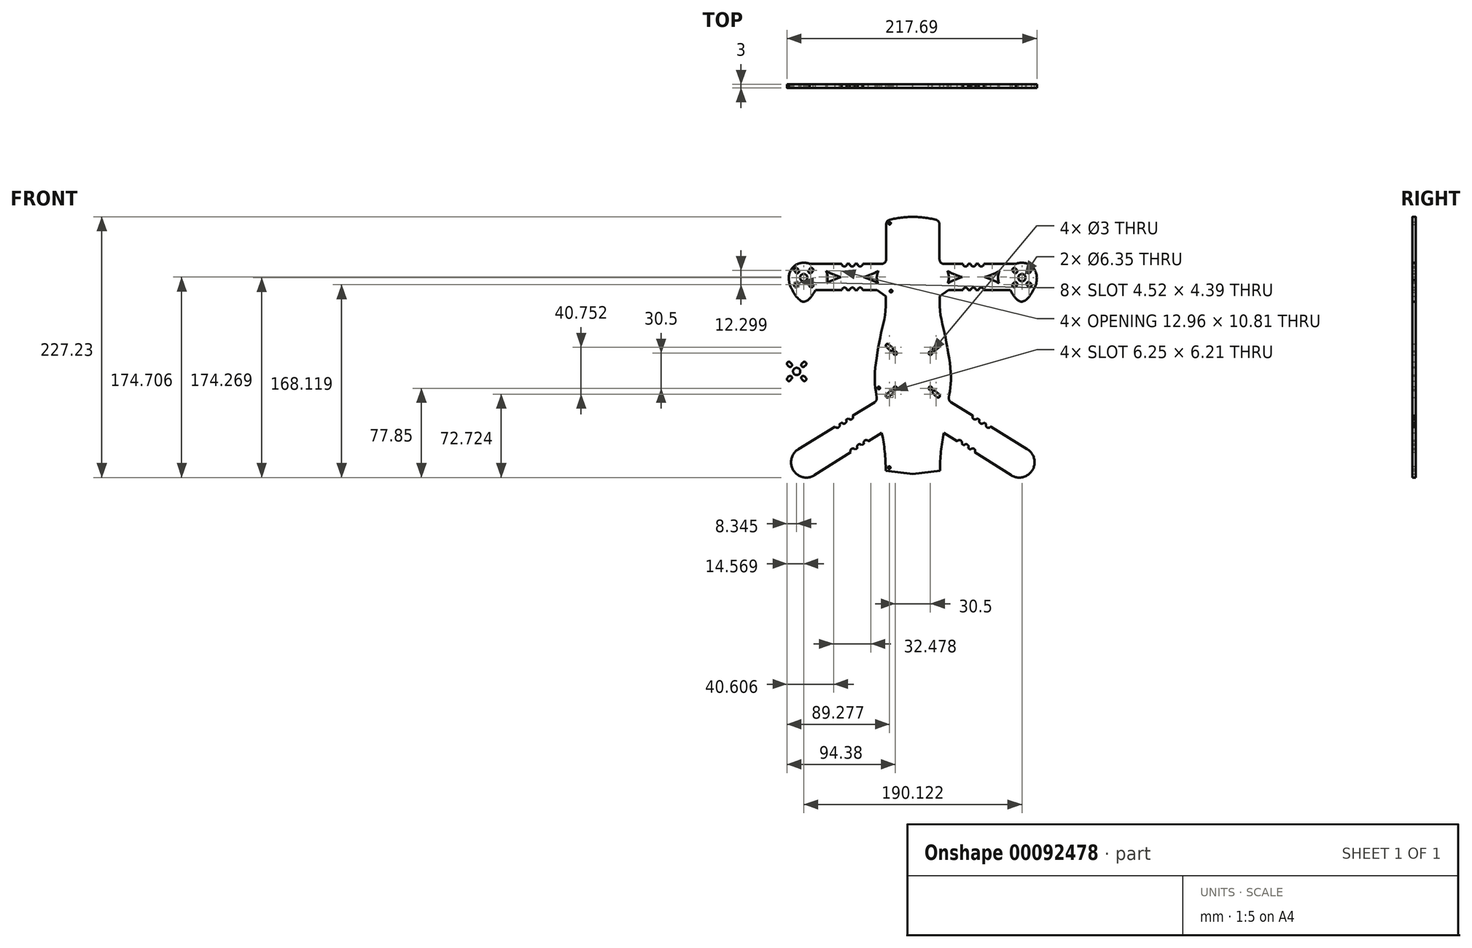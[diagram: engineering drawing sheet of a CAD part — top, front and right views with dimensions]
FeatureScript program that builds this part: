
annotation { "Feature Type Name" : "Feature", "Feature Type Description" : "" }
export const myFeature = defineFeature(function(context is Context, id is Id, definition is map)
    precondition{}
    {
        {
            var Q0;
            Q0=qCreatedBy(makeId("Front.planeOp"),FACE);
            var sketch = newSketch(context, id + "F0", { "sketchPlane" : qUnion([Q0])});
            skArc(sketch, "E0", {"start": v(-89.84, 93.07) * mm, "mid": v(-102.97, 91.49) * mm, "end": v(-107.91, 79.22) * mm});
            skLineSegment(sketch, "E1", {"start": v(-89.84, 93.07) * mm, "end": v(-68.74, 93.07) * mm});
            skLineSegment(sketch, "E2", {"start": v(-84.98, 70.21) * mm, "end": v(-68.66, 70.21) * mm});
            skCircle(sketch, "E3", {"center": v(-95.06, 81.17) * mm, "radius": 63.5 * mm, "construction": true});
            skCircle(sketch, "E4", {"center": v(-92.79, -79.8) * mm, "radius": 63.5 * mm, "construction": true});
            skLineSegment(sketch, "E5.trimOffspring", {"start": v(-27, 67.39) * mm, "end": v(-27, 67.4) * mm});
            skArc(sketch, "E6", {"start": v(0, 134.13) * mm, "mid": v(-10.16, 133.5) * mm, "end": v(-20.15, 131.58) * mm});
            skLineSegment(sketch, "E7", {"start": v(-104.2, 69.27) * mm, "end": v(-104.2, 69.27) * mm});
            skFitSpline(sketch, "E8.trimOffspring", {"points": [v(-82.06, 81.17) * mm, v(-83.74, 72.94) * mm, v(-95.05, 60.22) * mm, v(-105.53, 73.45) * mm, v(-110.06, 81.17) * mm], "startDerivative": vector(-2.07, -33.38) * mm, "endDerivative": vector(-8.03, 30.88) * mm});
            skFitSpline(sketch, "E9.MirrorCS", {"points": [v(-107.91, 79.22) * mm, v(-106.3, 72.94) * mm, v(-95.05, 60.22) * mm, v(-84.6, 73.45) * mm, v(-82.06, 81.17) * mm], "startDerivative": vector(2.07, -33.38) * mm, "endDerivative": vector(8.03, 30.88) * mm});
            skLineSegment(sketch, "E10.trimOffspring", {"start": v(-95.06, 68.17) * mm, "end": v(-95.06, 68.16) * mm});
            skLineSegment(sketch, "E11.trimOffspring", {"start": v(-102.98, 70.86) * mm, "end": v(-102.98, 70.86) * mm});
            skFitSpline(sketch, "E12.trimOffspring", {"points": [v(-82.07, 81.2) * mm, v(-83.75, 72.93) * mm, v(-95.05, 60.22) * mm, v(-105.53, 73.45) * mm, v(-108.06, 81.16) * mm], "startDerivative": vector(-2.07, -33.38) * mm, "endDerivative": vector(-8.03, 30.88) * mm});
            skPoint(sketch, "E13.visualSharp", {"position": v(-27.02, 93.07) * mm});
            skArc(sketch, "E13.filletArc", {"start": v(-27.02, 96.91) * mm, "mid": v(-27.02, 97) * mm, "end": v(-27.02, 97.07) * mm});
            skLineSegment(sketch, "E14.MirrorCS", {"start": v(27.02, 126.57) * mm, "end": v(27.02, 126.57) * mm});
            skLineSegment(sketch, "E15.MirrorCS", {"start": v(25.72, 29.34) * mm, "end": v(25.72, 29.34) * mm});
            skCircle(sketch, "E16.MirrorC", {"center": v(92.79, -79.8) * mm, "radius": 63.5 * mm, "construction": true});
            skLineSegment(sketch, "E17.MirrorCS", {"start": v(33.17, -57.94) * mm, "end": v(30.27, -56.1) * mm});
            skArc(sketch, "E18.MirrorCS", {"start": v(99.78, -68.48) * mm, "mid": v(104.07, -86.84) * mm, "end": v(85.7, -91.05) * mm});
            skCircle(sketch, "E19.MirrorC", {"center": v(95.06, 81.17) * mm, "radius": 63.5 * mm, "construction": true});
            skPoint(sketch, "E20.end.orphan", {"position": v(0, 134.13) * mm});
            skArc(sketch, "E21", {"start": v(-55, 93.07) * mm, "mid": v(-52.79, 90.85) * mm, "end": v(-50.56, 93.07) * mm});
            skArc(sketch, "E22", {"start": v(-61.87, 93.07) * mm, "mid": v(-59.65, 90.85) * mm, "end": v(-57.43, 93.07) * mm});
            skPoint(sketch, "E23.center.orphan", {"position": v(-59.65, 92.47) * mm});
            skLineSegment(sketch, "E24.trimOffspring", {"start": v(-64.3, 93.07) * mm, "end": v(-61.87, 93.07) * mm});
            skLineSegment(sketch, "E25.trimOffspring", {"start": v(-57.43, 93.07) * mm, "end": v(-55, 93.07) * mm});
            skCircle(sketch, "E26", {"center": v(-37.46, 81.64) * mm, "radius": 13.12 * mm, "construction": true});
            skPoint(sketch, "E26.second.point", {"position": v(-31.02, 70.21) * mm});
            skPoint(sketch, "E26.third.point", {"position": v(-50.56, 82.35) * mm});
            skArc(sketch, "E27.MirrorCS", {"start": v(-61.79, 70.21) * mm, "mid": v(-59.56, 72.44) * mm, "end": v(-57.34, 70.21) * mm});
            skArc(sketch, "E28.MirrorCS", {"start": v(-54.92, 70.21) * mm, "mid": v(-52.7, 72.44) * mm, "end": v(-50.48, 70.21) * mm});
            skLineSegment(sketch, "E29.trimOffspring", {"start": v(-64.2, 70.21) * mm, "end": v(-61.79, 70.21) * mm});
            skLineSegment(sketch, "E30.trimOffspring", {"start": v(-57.34, 70.21) * mm, "end": v(-54.92, 70.21) * mm});
            skLineSegment(sketch, "E31.trimOffspring", {"start": v(-50.48, 70.21) * mm, "end": v(-48.14, 70.21) * mm});
            skLineSegment(sketch, "E32.MirrorCS", {"start": v(-99.78, -68.48) * mm, "end": v(-73.61, -52.32) * mm});
            skLineSegment(sketch, "E33.MirrorCS", {"start": v(-85.7, -91.05) * mm, "end": v(-59.85, -74.76) * mm});
            skArc(sketch, "E34.MirrorCS", {"start": v(-99.78, -68.48) * mm, "mid": v(-104.07, -86.84) * mm, "end": v(-85.7, -91.05) * mm});
            skArc(sketch, "E35", {"start": v(-67.78, -48.72) * mm, "mid": v(-64.72, -49.44) * mm, "end": v(-64, -46.38) * mm});
            skArc(sketch, "E36", {"start": v(-61.94, -45.11) * mm, "mid": v(-58.88, -45.83) * mm, "end": v(-58.15, -42.77) * mm});
            skLineSegment(sketch, "E37.trimOffspring", {"start": v(-64, -46.38) * mm, "end": v(-61.94, -45.11) * mm});
            skLineSegment(sketch, "E38.trimOffspring", {"start": v(-69.83, -49.98) * mm, "end": v(-67.78, -48.72) * mm});
            skLineSegment(sketch, "E39.trimOffspring", {"start": v(-58.15, -42.77) * mm, "end": v(-56.1, -41.5) * mm});
            skArc(sketch, "E40.MirrorCS", {"start": v(-54.05, -71.1) * mm, "mid": v(-53.34, -68.05) * mm, "end": v(-50.29, -68.73) * mm});
            skArc(sketch, "E41.MirrorCS", {"start": v(-48.24, -67.44) * mm, "mid": v(-47.54, -64.4) * mm, "end": v(-44.48, -65.07) * mm});
            skLineSegment(sketch, "E42.trimOffspring", {"start": v(-56.09, -72.39) * mm, "end": v(-54.05, -71.1) * mm});
            skLineSegment(sketch, "E43.trimOffspring", {"start": v(-50.29, -68.73) * mm, "end": v(-48.24, -67.44) * mm});
            skLineSegment(sketch, "E44.trimOffspring", {"start": v(-44.48, -65.07) * mm, "end": v(-42.46, -63.8) * mm});
            skArc(sketch, "E45.MirrorCS", {"start": v(61.94, -45.11) * mm, "mid": v(58.88, -45.83) * mm, "end": v(58.15, -42.77) * mm});
            skLineSegment(sketch, "E46.MirrorCS", {"start": v(64, -46.38) * mm, "end": v(61.94, -45.11) * mm});
            skArc(sketch, "E47.MirrorCS", {"start": v(67.78, -48.72) * mm, "mid": v(64.72, -49.44) * mm, "end": v(64, -46.38) * mm});
            skLineSegment(sketch, "E48.MirrorCS", {"start": v(69.83, -49.98) * mm, "end": v(67.78, -48.72) * mm});
            skLineSegment(sketch, "E49.MirrorCS", {"start": v(99.78, -68.48) * mm, "end": v(73.61, -52.32) * mm});
            skLineSegment(sketch, "E50.MirrorCS", {"start": v(44.48, -65.07) * mm, "end": v(42.46, -63.8) * mm});
            skArc(sketch, "E51.MirrorCS", {"start": v(48.24, -67.44) * mm, "mid": v(47.54, -64.4) * mm, "end": v(44.48, -65.07) * mm});
            skLineSegment(sketch, "E52.MirrorCS", {"start": v(50.29, -68.73) * mm, "end": v(48.24, -67.44) * mm});
            skArc(sketch, "E53.MirrorCS", {"start": v(54.05, -71.1) * mm, "mid": v(53.34, -68.05) * mm, "end": v(50.29, -68.73) * mm});
            skLineSegment(sketch, "E54.MirrorCS", {"start": v(56.09, -72.39) * mm, "end": v(54.05, -71.1) * mm});
            skLineSegment(sketch, "E55.MirrorCS", {"start": v(85.7, -91.05) * mm, "end": v(59.85, -74.76) * mm});
            skLineSegment(sketch, "E56.MirrorCS", {"start": v(-27.02, -119.64) * mm, "end": v(-26.92, -119.64) * mm});
            skLineSegment(sketch, "E57", {"start": v(0, -156.72) * mm, "end": v(0, 138.64) * mm, "construction": true});
            skLineSegment(sketch, "E58.MirrorCS", {"start": v(50.48, 70.21) * mm, "end": v(48.14, 70.21) * mm});
            skArc(sketch, "E59.MirrorCS", {"start": v(54.92, 70.21) * mm, "mid": v(52.7, 72.44) * mm, "end": v(50.48, 70.21) * mm});
            skLineSegment(sketch, "E60.MirrorCS", {"start": v(57.34, 70.21) * mm, "end": v(54.92, 70.21) * mm});
            skArc(sketch, "E61.MirrorCS", {"start": v(61.79, 70.21) * mm, "mid": v(59.56, 72.44) * mm, "end": v(57.34, 70.21) * mm});
            skLineSegment(sketch, "E62.MirrorCS", {"start": v(64.2, 70.21) * mm, "end": v(61.79, 70.21) * mm});
            skLineSegment(sketch, "E63.MirrorCS", {"start": v(84.98, 70.21) * mm, "end": v(68.66, 70.21) * mm});
            skFitSpline(sketch, "E64.MirrorCS", {"points": [v(82.07, 81.2) * mm, v(83.75, 72.93) * mm, v(95.05, 60.22) * mm, v(105.53, 73.45) * mm, v(108.06, 81.16) * mm], "startDerivative": vector(2.07, -33.38) * mm, "endDerivative": vector(8.03, 30.88) * mm});
            skFitSpline(sketch, "E65.MirrorCS", {"points": [v(107.91, 79.22) * mm, v(106.3, 72.94) * mm, v(95.05, 60.22) * mm, v(84.6, 73.45) * mm, v(82.06, 81.17) * mm], "startDerivative": vector(-2.07, -33.38) * mm, "endDerivative": vector(-8.03, 30.88) * mm});
            skArc(sketch, "E66.MirrorCS", {"start": v(89.84, 93.07) * mm, "mid": v(102.97, 91.49) * mm, "end": v(107.91, 79.22) * mm});
            skLineSegment(sketch, "E67.MirrorCS", {"start": v(89.84, 93.07) * mm, "end": v(68.74, 93.07) * mm});
            skLineSegment(sketch, "E68.MirrorCS", {"start": v(64.3, 93.07) * mm, "end": v(61.87, 93.07) * mm});
            skArc(sketch, "E69.MirrorCS", {"start": v(61.87, 93.07) * mm, "mid": v(59.65, 90.85) * mm, "end": v(57.43, 93.07) * mm});
            skLineSegment(sketch, "E70.MirrorCS", {"start": v(57.43, 93.07) * mm, "end": v(55, 93.07) * mm});
            skArc(sketch, "E71.MirrorCS", {"start": v(55, 93.07) * mm, "mid": v(52.79, 90.85) * mm, "end": v(50.56, 93.07) * mm});
            skLineSegment(sketch, "E72.MirrorCS", {"start": v(50.56, 93.07) * mm, "end": v(48.14, 93.07) * mm});
            skLineSegment(sketch, "E73", {"start": v(-27, 67.4) * mm, "end": v(-31.02, 70.21) * mm});
            skLineSegment(sketch, "E74.MirrorCS", {"start": v(27, 67.4) * mm, "end": v(31.02, 70.21) * mm});
            skLineSegment(sketch, "E75.trimOffspring", {"start": v(27, 70.21) * mm, "end": v(26.91, 70.21) * mm});
            skLineSegment(sketch, "E76.trimOffspring", {"start": v(27, 70.21) * mm, "end": v(27, 70.21) * mm});
            skLineSegment(sketch, "E77.bottom", {"start": v(-15.25, -15.25) * mm, "end": v(15.25, -15.25) * mm, "construction": true});
            skLineSegment(sketch, "E77.top", {"start": v(-15.25, 15.25) * mm, "end": v(15.25, 15.25) * mm, "construction": true});
            skLineSegment(sketch, "E77.left", {"start": v(-15.25, -15.25) * mm, "end": v(-15.25, 15.25) * mm, "construction": true});
            skLineSegment(sketch, "E77.right", {"start": v(15.25, -15.25) * mm, "end": v(15.25, 15.25) * mm, "construction": true});
            skPoint(sketch, "E77.middle", {"position": v(0, 0) * mm});
            skCircle(sketch, "E78", {"center": v(-15.25, 15.25) * mm, "radius": 1.5 * mm});
            skCircle(sketch, "E79", {"center": v(-15.25, -15.25) * mm, "radius": 1.5 * mm});
            skCircle(sketch, "E80", {"center": v(15.25, -15.25) * mm, "radius": 1.5 * mm});
            skCircle(sketch, "E81", {"center": v(15.25, 15.25) * mm, "radius": 1.5 * mm});
            skPoint(sketch, "E82.orphan", {"position": v(27, 67.4) * mm});
            skLineSegment(sketch, "E83", {"start": v(-33.17, -57.94) * mm, "end": v(-27, -54.05) * mm});
            skLineSegment(sketch, "E84", {"start": v(-39.84, -31.46) * mm, "end": v(-33.24, -27.38) * mm});
            skLineSegment(sketch, "E85", {"start": v(-27, 67.4) * mm, "end": v(-23.43, 64.9) * mm});
            skLineSegment(sketch, "E86", {"start": v(-31.02, 93.07) * mm, "end": v(-27.28, 93.07) * mm});
            skArc(sketch, "E87", {"start": v(-27, -120.02) * mm, "mid": v(-26.96, -119.83) * mm, "end": v(-26.92, -119.64) * mm});
            skFitSpline(sketch, "E88", {"points": [v(-30.93, -25.96) * mm, v(-31.88, -20.43) * mm, v(-32.97, -11.05) * mm, v(-32.97, 0) * mm, v(-30.51, 17.65) * mm, v(-27.02, 35.59) * mm, v(-24.06, 49.37) * mm, v(-23.43, 65.59) * mm], "startDerivative": vector(-9.96, 54.34) * mm, "endDerivative": vector(-0.3, 104.07) * mm});
            skLineSegment(sketch, "E89", {"start": v(-23.29, 97.04) * mm, "end": v(-23.14, 127.74) * mm});
            skPoint(sketch, "E89.startSnap0", {"position": v(-29, 68.8) * mm});
            skPoint(sketch, "E90.filletArc.center.orphan", {"position": v(-23.02, 126.6) * mm});
            skPoint(sketch, "E91.end.orphan", {"position": v(-27.02, 126.57) * mm});
            skPoint(sketch, "E92.newPointB", {"position": v(-23.43, 68.8) * mm});
            skArc(sketch, "E92.filletArc", {"start": v(-27.28, 93.07) * mm, "mid": v(-24.46, 94.23) * mm, "end": v(-23.29, 97.04) * mm});
            skArc(sketch, "E93.filletArc", {"start": v(-20.15, 131.58) * mm, "mid": v(-22.3, 130.17) * mm, "end": v(-23.14, 127.74) * mm});
            skPoint(sketch, "E94.0.internal.orphan", {"position": v(-26.91, 70.21) * mm});
            skPoint(sketch, "E94.7.internal.orphan", {"position": v(-32.97, -21.49) * mm});
            skPoint(sketch, "E94.8.internal.orphan", {"position": v(-26.91, -50.04) * mm});
            skPoint(sketch, "E95.startSnap0", {"position": v(-23.62, -87.03) * mm});
            skArc(sketch, "E96.trimOffspring", {"start": v(-23.62, -87.03) * mm, "mid": v(-24.47, -70.45) * mm, "end": v(-27, -54.05) * mm});
            skPoint(sketch, "E97.MirrorCS.end.orphan", {"position": v(0, -119.64) * mm});
            skPoint(sketch, "E98.orphan", {"position": v(27.02, 97.07) * mm});
            skPoint(sketch, "E99.MirrorCS.start.orphan", {"position": v(31.02, 93.07) * mm});
            skLineSegment(sketch, "E100.MirrorCS", {"start": v(39.84, -31.46) * mm, "end": v(33.24, -27.38) * mm});
            skArc(sketch, "E101.MirrorCS", {"start": v(23.62, -87.03) * mm, "mid": v(24.47, -70.45) * mm, "end": v(27, -54.05) * mm});
            skLineSegment(sketch, "E102.MirrorCS", {"start": v(33.17, -57.94) * mm, "end": v(27, -54.05) * mm});
            skFitSpline(sketch, "E103.MirrorCS", {"points": [v(30.93, -25.96) * mm, v(31.88, -20.43) * mm, v(32.97, -11.05) * mm, v(32.97, 0) * mm, v(30.51, 17.65) * mm, v(27.02, 35.59) * mm, v(24.06, 49.37) * mm, v(23.43, 65.59) * mm], "startDerivative": vector(9.96, 54.34) * mm, "endDerivative": vector(0.3, 104.07) * mm});
            skLineSegment(sketch, "E104.MirrorCS", {"start": v(27, 67.4) * mm, "end": v(23.43, 64.9) * mm});
            skArc(sketch, "E105.MirrorCS", {"start": v(27.28, 93.07) * mm, "mid": v(24.46, 94.23) * mm, "end": v(23.29, 97.04) * mm});
            skLineSegment(sketch, "E106.MirrorCS", {"start": v(23.29, 97.04) * mm, "end": v(23.14, 127.74) * mm});
            skArc(sketch, "E107.MirrorCS", {"start": v(0, 134.13) * mm, "mid": v(10.16, 133.5) * mm, "end": v(20.15, 131.58) * mm});
            skArc(sketch, "E108.MirrorCS", {"start": v(20.15, 131.58) * mm, "mid": v(22.3, 130.17) * mm, "end": v(23.14, 127.74) * mm});
            skLineSegment(sketch, "E109.MirrorCS", {"start": v(31.02, 93.07) * mm, "end": v(27.28, 93.07) * mm});
            skPoint(sketch, "E110.orphan", {"position": v(24.14, -87.03) * mm});
            skLineSegment(sketch, "E111", {"start": v(-23.62, -87.03) * mm, "end": v(0, -90.1) * mm});
            skLineSegment(sketch, "E112", {"start": v(0, -90.1) * mm, "end": v(23.62, -87.03) * mm});
            skArc(sketch, "E113.filletArc", {"start": v(-33.24, -27.38) * mm, "mid": v(-31.7, -25.63) * mm, "end": v(-31.4, -23.3) * mm});
            skArc(sketch, "E114.filletArc", {"start": v(31.4, -23.3) * mm, "mid": v(31.7, -25.63) * mm, "end": v(33.24, -27.38) * mm});
            skLineSegment(sketch, "E115.bottom", {"start": v(-101.78, 74.46) * mm, "end": v(-88.34, 74.46) * mm, "construction": true});
            skLineSegment(sketch, "E115.top", {"start": v(-101.78, 87.88) * mm, "end": v(-88.34, 87.88) * mm, "construction": true});
            skLineSegment(sketch, "E115.left", {"start": v(-101.78, 74.46) * mm, "end": v(-101.78, 87.88) * mm, "construction": true});
            skLineSegment(sketch, "E115.right", {"start": v(-88.34, 74.46) * mm, "end": v(-88.34, 87.88) * mm, "construction": true});
            skArc(sketch, "E116", {"start": v(-100.5, 89) * mm, "mid": v(-102.9, 89.16) * mm, "end": v(-103.06, 86.76) * mm});
            skArc(sketch, "E117", {"start": v(-89.61, 73.33) * mm, "mid": v(-87.21, 73.18) * mm, "end": v(-87.07, 75.58) * mm});
            skArc(sketch, "E118", {"start": v(-103.06, 75.58) * mm, "mid": v(-102.9, 73.18) * mm, "end": v(-100.5, 73.33) * mm});
            skCircle(sketch, "E119", {"center": v(-95.06, 81.17) * mm, "radius": 3.18 * mm});
            skArc(sketch, "E120", {"start": v(-102.06, 85.63) * mm, "mid": v(-99.66, 85.48) * mm, "end": v(-99.51, 87.88) * mm});
            skArc(sketch, "E121", {"start": v(-90.6, 87.88) * mm, "mid": v(-90.46, 85.48) * mm, "end": v(-88.06, 85.63) * mm});
            skArc(sketch, "E122", {"start": v(-99.51, 74.46) * mm, "mid": v(-99.66, 76.86) * mm, "end": v(-102.06, 76.7) * mm});
            skArc(sketch, "E123", {"start": v(-88.06, 76.7) * mm, "mid": v(-90.46, 76.86) * mm, "end": v(-90.6, 74.46) * mm});
            skLineSegment(sketch, "E124", {"start": v(-103.06, 75.58) * mm, "end": v(-102.06, 76.7) * mm});
            skLineSegment(sketch, "E125", {"start": v(-100.5, 73.33) * mm, "end": v(-99.51, 74.46) * mm});
            skLineSegment(sketch, "E126", {"start": v(-88.06, 76.7) * mm, "end": v(-87.07, 75.58) * mm});
            skLineSegment(sketch, "E127", {"start": v(-90.6, 74.46) * mm, "end": v(-89.61, 73.33) * mm});
            skLineSegment(sketch, "E128", {"start": v(-90.6, 87.88) * mm, "end": v(-89.52, 89.11) * mm});
            skLineSegment(sketch, "E129", {"start": v(-88.06, 85.63) * mm, "end": v(-87.07, 86.76) * mm});
            skLineSegment(sketch, "E130", {"start": v(-103.06, 86.76) * mm, "end": v(-102.06, 85.63) * mm});
            skLineSegment(sketch, "E131", {"start": v(-100.5, 89) * mm, "end": v(-99.51, 87.88) * mm});
            skArc(sketch, "E132.trimOffspring", {"start": v(-87.07, 86.76) * mm, "mid": v(-87.21, 89.16) * mm, "end": v(-89.61, 89) * mm});
            skLineSegment(sketch, "E133.MirrorCS", {"start": v(90.6, 87.88) * mm, "end": v(89.52, 89.11) * mm});
            skLineSegment(sketch, "E134.MirrorCS", {"start": v(88.06, 85.63) * mm, "end": v(87.07, 86.76) * mm});
            skArc(sketch, "E135.MirrorCS", {"start": v(87.07, 86.76) * mm, "mid": v(87.21, 89.16) * mm, "end": v(89.61, 89) * mm});
            skArc(sketch, "E136.MirrorCS", {"start": v(90.6, 87.88) * mm, "mid": v(90.46, 85.48) * mm, "end": v(88.06, 85.63) * mm});
            skArc(sketch, "E137.MirrorCS", {"start": v(88.06, 76.7) * mm, "mid": v(90.46, 76.86) * mm, "end": v(90.6, 74.46) * mm});
            skArc(sketch, "E138.MirrorCS", {"start": v(89.61, 73.33) * mm, "mid": v(87.21, 73.18) * mm, "end": v(87.07, 75.58) * mm});
            skLineSegment(sketch, "E139.MirrorCS", {"start": v(88.06, 76.7) * mm, "end": v(87.07, 75.58) * mm});
            skLineSegment(sketch, "E140.MirrorCS", {"start": v(90.6, 74.46) * mm, "end": v(89.61, 73.33) * mm});
            skLineSegment(sketch, "E141.MirrorCS", {"start": v(100.5, 73.33) * mm, "end": v(99.51, 74.46) * mm});
            skLineSegment(sketch, "E142.MirrorCS", {"start": v(103.06, 75.58) * mm, "end": v(102.06, 76.7) * mm});
            skArc(sketch, "E143.MirrorCS", {"start": v(99.51, 74.46) * mm, "mid": v(99.66, 76.86) * mm, "end": v(102.06, 76.7) * mm});
            skArc(sketch, "E144.MirrorCS", {"start": v(103.06, 75.58) * mm, "mid": v(102.9, 73.18) * mm, "end": v(100.5, 73.33) * mm});
            skArc(sketch, "E145.MirrorCS", {"start": v(102.06, 85.63) * mm, "mid": v(99.66, 85.48) * mm, "end": v(99.51, 87.88) * mm});
            skArc(sketch, "E146.MirrorCS", {"start": v(100.5, 89) * mm, "mid": v(102.9, 89.16) * mm, "end": v(103.06, 86.76) * mm});
            skLineSegment(sketch, "E147.MirrorCS", {"start": v(103.06, 86.76) * mm, "end": v(102.06, 85.63) * mm});
            skLineSegment(sketch, "E148.MirrorCS", {"start": v(100.5, 89) * mm, "end": v(99.51, 87.88) * mm});
            skCircle(sketch, "E149.MirrorC", {"center": v(95.06, 81.17) * mm, "radius": 3.18 * mm});
            skArc(sketch, "E150", {"start": v(-48.14, 93.07) * mm, "mid": v(-45.92, 90.85) * mm, "end": v(-43.7, 93.07) * mm});
            skLineSegment(sketch, "E151.trimOffspring", {"start": v(-43.7, 93.07) * mm, "end": v(-31.02, 93.07) * mm});
            skLineSegment(sketch, "E152", {"start": v(-50.56, 93.07) * mm, "end": v(-48.14, 93.07) * mm});
            skLineSegment(sketch, "E153", {"start": v(-64.3, 93.07) * mm, "end": v(-68.74, 93.07) * mm});
            skLineSegment(sketch, "E154", {"start": v(-68.66, 70.21) * mm, "end": v(-64.2, 70.21) * mm});
            skArc(sketch, "E155.MirrorCS", {"start": v(-48.14, 70.21) * mm, "mid": v(-45.92, 72.44) * mm, "end": v(-43.7, 70.21) * mm});
            skLineSegment(sketch, "E156.trimOffspring", {"start": v(-43.9, 70.21) * mm, "end": v(-31.02, 70.21) * mm});
            skPoint(sketch, "E157.startSnap0", {"position": v(-56.22, 93.07) * mm});
            skArc(sketch, "E158.MirrorCS", {"start": v(-30.44, 76.2) * mm, "mid": v(-31.34, 81.64) * mm, "end": v(-30.07, 87) * mm});
            skArc(sketch, "E159.MirrorCS", {"start": v(-30.07, 87) * mm, "mid": v(-36.38, 83.91) * mm, "end": v(-43.02, 81.64) * mm});
            skArc(sketch, "E160.MirrorCS", {"start": v(-43.02, 81.64) * mm, "mid": v(-36.56, 79.32) * mm, "end": v(-30.44, 76.2) * mm});
            skArc(sketch, "E161.MirrorCS", {"start": v(-62.55, 81.64) * mm, "mid": v(-69.01, 79.32) * mm, "end": v(-75.14, 76.2) * mm});
            skArc(sketch, "E162.MirrorCS", {"start": v(-75.5, 87) * mm, "mid": v(-69.2, 83.91) * mm, "end": v(-62.55, 81.64) * mm});
            skArc(sketch, "E163.MirrorCS", {"start": v(-75.14, 76.2) * mm, "mid": v(-74.23, 81.64) * mm, "end": v(-75.5, 87) * mm});
            skArc(sketch, "E164.MirrorCS", {"start": v(30.07, 87) * mm, "mid": v(36.38, 83.91) * mm, "end": v(43.02, 81.64) * mm});
            skArc(sketch, "E165.MirrorCS", {"start": v(43.02, 81.64) * mm, "mid": v(36.56, 79.32) * mm, "end": v(30.44, 76.2) * mm});
            skArc(sketch, "E166.MirrorCS", {"start": v(30.44, 76.2) * mm, "mid": v(31.34, 81.64) * mm, "end": v(30.07, 87) * mm});
            skArc(sketch, "E167.MirrorCS", {"start": v(75.5, 87) * mm, "mid": v(69.2, 83.91) * mm, "end": v(62.55, 81.64) * mm});
            skArc(sketch, "E168.MirrorCS", {"start": v(62.55, 81.64) * mm, "mid": v(69.01, 79.32) * mm, "end": v(75.14, 76.2) * mm});
            skArc(sketch, "E169.MirrorCS", {"start": v(75.14, 76.2) * mm, "mid": v(74.23, 81.64) * mm, "end": v(75.5, 87) * mm});
            skArc(sketch, "E170.MirrorCS", {"start": v(48.14, 93.07) * mm, "mid": v(45.92, 90.85) * mm, "end": v(43.7, 93.07) * mm});
            skArc(sketch, "E171.MirrorCS", {"start": v(48.14, 70.21) * mm, "mid": v(45.92, 72.44) * mm, "end": v(43.7, 70.21) * mm});
            skLineSegment(sketch, "E172", {"start": v(64.2, 70.21) * mm, "end": v(68.66, 70.21) * mm});
            skLineSegment(sketch, "E173", {"start": v(64.3, 93.07) * mm, "end": v(68.74, 93.07) * mm});
            skLineSegment(sketch, "E174.trimOffspring", {"start": v(43.7, 93.07) * mm, "end": v(31.02, 93.07) * mm});
            skLineSegment(sketch, "E175.trimOffspring", {"start": v(43.7, 70.21) * mm, "end": v(31.02, 70.21) * mm});
            skArc(sketch, "E176", {"start": v(-56.11, -41.49) * mm, "mid": v(-53.05, -42.24) * mm, "end": v(-52.32, -39.17) * mm});
            skLineSegment(sketch, "E177.trimOffspring", {"start": v(-52.32, -39.17) * mm, "end": v(-36.47, -29.38) * mm});
            skLineSegment(sketch, "E178", {"start": v(-73.61, -52.32) * mm, "end": v(-69.83, -49.98) * mm});
            skArc(sketch, "E179.MirrorCS", {"start": v(-42.46, -63.8) * mm, "mid": v(-41.77, -60.73) * mm, "end": v(-38.7, -61.43) * mm});
            skPoint(sketch, "E180.orphan", {"position": v(-42.32, -64) * mm});
            skLineSegment(sketch, "E181", {"start": v(-59.85, -74.76) * mm, "end": v(-56.09, -72.39) * mm});
            skLineSegment(sketch, "E182.trimOffspring", {"start": v(-38.7, -61.43) * mm, "end": v(-30.27, -56.1) * mm});
            skArc(sketch, "E183.MirrorCS", {"start": v(56.11, -41.49) * mm, "mid": v(53.05, -42.24) * mm, "end": v(52.32, -39.17) * mm});
            skArc(sketch, "E184.MirrorCS", {"start": v(42.46, -63.8) * mm, "mid": v(41.77, -60.73) * mm, "end": v(38.7, -61.43) * mm});
            skLineSegment(sketch, "E185", {"start": v(56.09, -72.39) * mm, "end": v(59.85, -74.76) * mm});
            skLineSegment(sketch, "E186", {"start": v(69.83, -49.98) * mm, "end": v(73.61, -52.32) * mm});
            skLineSegment(sketch, "E187.trimOffspring", {"start": v(52.32, -39.17) * mm, "end": v(36.47, -29.38) * mm});
            skLineSegment(sketch, "E188.trimOffspring", {"start": v(38.7, -61.43) * mm, "end": v(30.27, -56.1) * mm});
            skLineSegment(sketch, "E189", {"start": v(58.15, -42.77) * mm, "end": v(56.11, -41.49) * mm});
            skLineSegment(sketch, "E190", {"start": v(-110.34, -12.48) * mm, "end": v(-110.34, -12.48) * mm});
            skLineSegment(sketch, "E191.trimOffspring", {"start": v(-109.12, -10.9) * mm, "end": v(-109.12, -10.9) * mm});
            skLineSegment(sketch, "E192.bottom", {"start": v(-107.93, -7.3) * mm, "end": v(-94.48, -7.3) * mm, "construction": true});
            skLineSegment(sketch, "E192.top", {"start": v(-107.93, 6.13) * mm, "end": v(-94.48, 6.13) * mm, "construction": true});
            skLineSegment(sketch, "E192.left", {"start": v(-107.93, -7.3) * mm, "end": v(-107.93, 6.13) * mm, "construction": true});
            skLineSegment(sketch, "E192.right", {"start": v(-94.48, -7.3) * mm, "end": v(-94.48, 6.13) * mm, "construction": true});
            skArc(sketch, "E193", {"start": v(-106.65, 7.26) * mm, "mid": v(-109.05, 7.4) * mm, "end": v(-109.2, 5) * mm});
            skArc(sketch, "E194", {"start": v(-95.75, -8.42) * mm, "mid": v(-93.36, -8.57) * mm, "end": v(-93.2, -6.17) * mm});
            skArc(sketch, "E195", {"start": v(-109.2, -6.17) * mm, "mid": v(-109.05, -8.57) * mm, "end": v(-106.65, -8.42) * mm});
            skCircle(sketch, "E196", {"center": v(-101.2, -0.58) * mm, "radius": 3.18 * mm});
            skArc(sketch, "E197", {"start": v(-108.2, 3.88) * mm, "mid": v(-105.8, 3.73) * mm, "end": v(-105.66, 6.13) * mm});
            skArc(sketch, "E198", {"start": v(-96.75, 6.13) * mm, "mid": v(-96.6, 3.73) * mm, "end": v(-94.2, 3.88) * mm});
            skArc(sketch, "E199", {"start": v(-105.66, -7.3) * mm, "mid": v(-105.8, -4.9) * mm, "end": v(-108.2, -5.04) * mm});
            skArc(sketch, "E200", {"start": v(-94.2, -5.04) * mm, "mid": v(-96.6, -4.9) * mm, "end": v(-96.75, -7.3) * mm});
            skLineSegment(sketch, "E201", {"start": v(-109.2, -6.17) * mm, "end": v(-108.2, -5.04) * mm});
            skLineSegment(sketch, "E202", {"start": v(-106.65, -8.42) * mm, "end": v(-105.66, -7.3) * mm});
            skLineSegment(sketch, "E203", {"start": v(-94.2, -5.04) * mm, "end": v(-93.2, -6.17) * mm});
            skLineSegment(sketch, "E204", {"start": v(-96.75, -7.3) * mm, "end": v(-95.75, -8.42) * mm});
            skLineSegment(sketch, "E205", {"start": v(-96.75, 6.13) * mm, "end": v(-95.66, 7.36) * mm});
            skLineSegment(sketch, "E206", {"start": v(-94.2, 3.88) * mm, "end": v(-93.2, 5) * mm});
            skLineSegment(sketch, "E207", {"start": v(-109.2, 5) * mm, "end": v(-108.2, 3.88) * mm});
            skLineSegment(sketch, "E208", {"start": v(-106.65, 7.26) * mm, "end": v(-105.66, 6.13) * mm});
            skArc(sketch, "E209.trimOffspring", {"start": v(-93.2, 5) * mm, "mid": v(-93.36, 7.4) * mm, "end": v(-95.75, 7.26) * mm});
            skCircle(sketch, "E210", {"center": v(-20.3, 128.6) * mm, "radius": 1.1 * mm});
            skCircle(sketch, "E211", {"center": v(-18.97, 69.42) * mm, "radius": 1.1 * mm});
            skCircle(sketch, "E212", {"center": v(-20.54, -84.44) * mm, "radius": 1.1 * mm});
            skCircle(sketch, "E213", {"center": v(-29.62, -15.05) * mm, "radius": 1.1 * mm});
            skLineSegment(sketch, "E214", {"start": v(0, 0) * mm, "end": v(24.04, 24.04) * mm, "construction": true});
            skLineSegment(sketch, "E215", {"start": v(0, 0) * mm, "end": v(-28.52, -28.52) * mm, "construction": true});
            skLineSegment(sketch, "E216", {"start": v(0, 0) * mm, "end": v(25.89, -25.89) * mm, "construction": true});
            skLineSegment(sketch, "E217", {"start": v(0, 0) * mm, "end": v(-24.83, 24.83) * mm, "construction": true});
            skLineSegment(sketch, "E218.bottom", {"start": v(-17.9, 17.9) * mm, "end": v(17.9, 17.9) * mm, "construction": true});
            skLineSegment(sketch, "E218.top", {"start": v(-17.9, -17.9) * mm, "end": v(17.9, -17.9) * mm, "construction": true});
            skLineSegment(sketch, "E218.left", {"start": v(-17.9, 17.9) * mm, "end": v(-17.9, -17.9) * mm, "construction": true});
            skLineSegment(sketch, "E218.right", {"start": v(17.9, 17.9) * mm, "end": v(17.9, -17.9) * mm, "construction": true});
            skArc(sketch, "E219", {"start": v(-19.78, 17.7) * mm, "mid": v(-17.66, 17.72) * mm, "end": v(-17.67, 19.84) * mm});
            skArc(sketch, "E220", {"start": v(-20.93, 23.05) * mm, "mid": v(-23.05, 23.03) * mm, "end": v(-23.03, 20.91) * mm});
            skLineSegment(sketch, "E221", {"start": v(-20.93, 23.05) * mm, "end": v(-17.67, 19.84) * mm});
            skLineSegment(sketch, "E222", {"start": v(-23.03, 20.91) * mm, "end": v(-19.78, 17.7) * mm});
            skLineSegment(sketch, "E223.MirrorCS", {"start": v(20.93, 23.05) * mm, "end": v(17.67, 19.84) * mm});
            skLineSegment(sketch, "E224.MirrorCS", {"start": v(23.03, 20.91) * mm, "end": v(19.78, 17.7) * mm});
            skArc(sketch, "E225.MirrorCS", {"start": v(20.93, 23.05) * mm, "mid": v(23.05, 23.03) * mm, "end": v(23.03, 20.91) * mm});
            skArc(sketch, "E226.MirrorCS", {"start": v(19.78, 17.7) * mm, "mid": v(17.66, 17.72) * mm, "end": v(17.67, 19.84) * mm});
            skLineSegment(sketch, "E227.MirrorCS", {"start": v(-23.03, -20.91) * mm, "end": v(-19.78, -17.7) * mm});
            skLineSegment(sketch, "E228.MirrorCS", {"start": v(-20.93, -23.05) * mm, "end": v(-17.67, -19.84) * mm});
            skArc(sketch, "E229.MirrorCS", {"start": v(-19.78, -17.7) * mm, "mid": v(-17.66, -17.72) * mm, "end": v(-17.67, -19.84) * mm});
            skArc(sketch, "E230.MirrorCS", {"start": v(-20.93, -23.05) * mm, "mid": v(-23.05, -23.03) * mm, "end": v(-23.03, -20.91) * mm});
            skLineSegment(sketch, "E231.MirrorCS", {"start": v(20.93, -23.05) * mm, "end": v(17.67, -19.84) * mm});
            skLineSegment(sketch, "E232.MirrorCS", {"start": v(23.03, -20.91) * mm, "end": v(19.78, -17.7) * mm});
            skArc(sketch, "E233.MirrorCS", {"start": v(19.78, -17.7) * mm, "mid": v(17.66, -17.72) * mm, "end": v(17.67, -19.84) * mm});
            skArc(sketch, "E234.MirrorCS", {"start": v(20.93, -23.05) * mm, "mid": v(23.05, -23.03) * mm, "end": v(23.03, -20.91) * mm});
            skSolve(sketch);
        }
        {
            var Q0;
            Q0=qSketchRegion(id+"F0",true);
            extrude(context, id + "F1", {"entities" : qUnion([Q0]), "depth" : 3 * mm});
        }
    });
